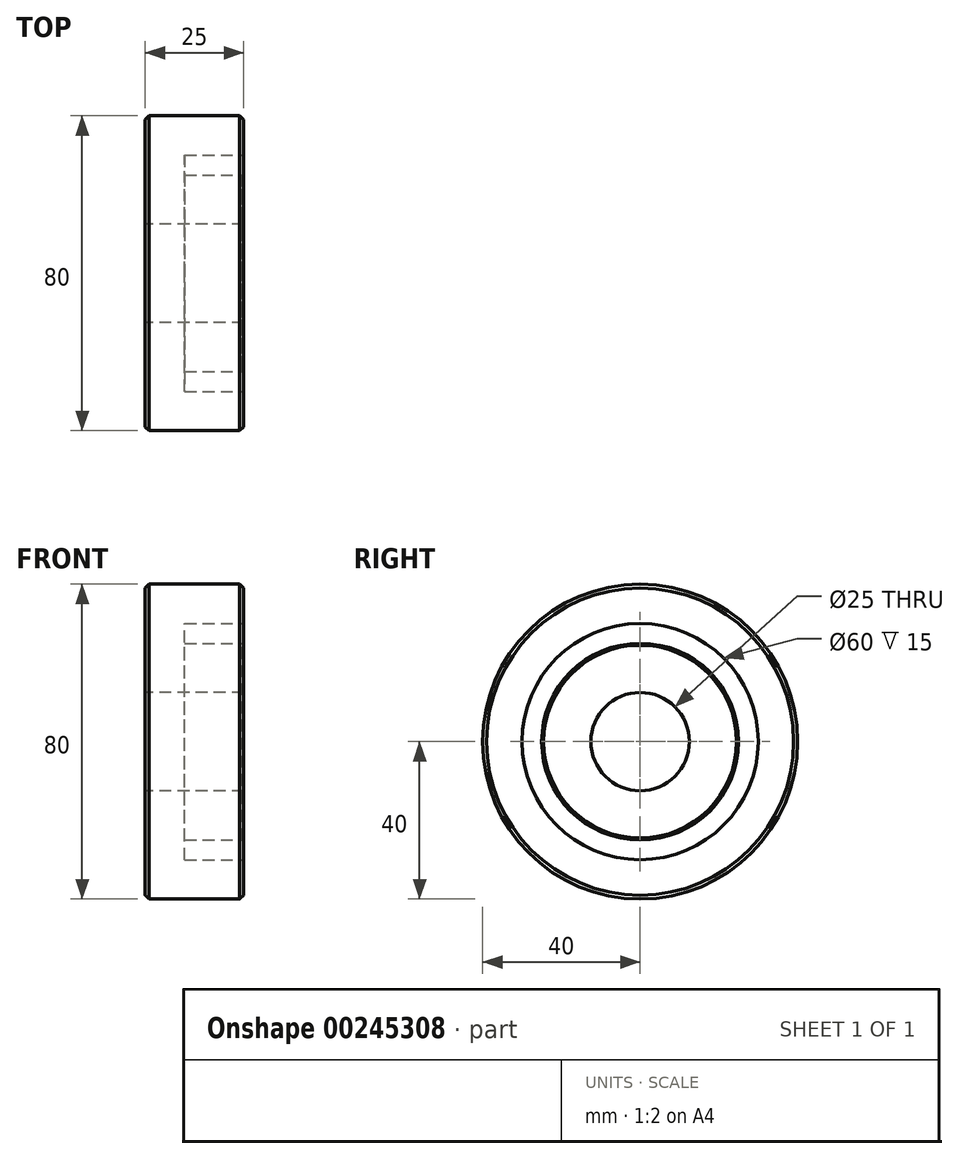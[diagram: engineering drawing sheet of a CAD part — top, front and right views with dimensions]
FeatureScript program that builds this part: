
annotation { "Feature Type Name" : "Feature", "Feature Type Description" : "" }
export const myFeature = defineFeature(function(context is Context, id is Id, definition is map)
    precondition{}
    {
        {
            var Q0;
            Q0=qCreatedBy(makeId("Right.planeOp"),FACE);
            var sketch = newSketch(context, id + "F0", { "sketchPlane" : qUnion([Q0])});
            skCircle(sketch, "E0", {"center": v(0, 0) * mm, "radius": 40 * mm});
            skSolve(sketch);
        }
        {
            var Q0;
            Q0 = qSketchRegion(id + "F0", true);
            extrude(context, id + "F1", {"entities" : qUnion([Q0]), "depth" : 25 * mm, "offsetDistance" : 25 * mm});
        }
        {
            var Q0;
            Q0=makeQuery(id+"F1.opExtrude","CAP_FACE",FACE,{"disambiguationData":[OSD([sQuery(id+"F0.wireOp",EDGE,"E0")])],"isStart":true});
            var sketch = newSketch(context, id + "F2", { "sketchPlane" : qUnion([Q0])});
            skCircle(sketch, "E1", {"center": v(0, 0) * mm, "radius": 12.5 * mm});
            skSolve(sketch);
        }
        {
            var Q0;
            Q0 = qSketchRegion(id + "F2", true);
            extrude(context, id + "F3", {"entities" : qUnion([Q0]), "operationType" : NewBodyOperationType.REMOVE, "endBound" : BoundingType.THROUGH_ALL, "oppositeDirection" : true, "depth" : 100 * mm, "offsetDistance" : 25 * mm});
        }
        {
            var Q0;
            Q0=makeQuery(id+"F3.opExtrude","CAP_EDGE",EDGE,{"disambiguationData":[OSD([sQuery(id+"F2.wireOp",EDGE,"E1")])],"isStart":false});
            var Q1;
            Q1=makeQuery(id+"F1.opExtrude","CAP_EDGE",EDGE,{"disambiguationData":[OSD([sQuery(id+"F0.wireOp",EDGE,"E0")])],"isStart":true});
            chamfer(context, id + "F4", {"entities" : qUnion([Q0, Q1]), "width" : 1 * mm, "tangentPropagation" : true});
        }
        {
            var Q0;
            Q0=makeQuery(id+"F1.opExtrude","CAP_FACE",FACE,{"disambiguationData":[OSD([sQuery(id+"F0.wireOp",EDGE,"E0")])],"isStart":false});
            var sketch = newSketch(context, id + "F5", { "sketchPlane" : qUnion([Q0])});
            skCircle(sketch, "E2", {"center": v(0, 0) * mm, "radius": 25 * mm});
            skCircle(sketch, "E3", {"center": v(0, 0) * mm, "radius": 30 * mm});
            skSolve(sketch);
        }
        {
            var Q0;
            Q0 = qSketchRegion(id + "F5", true);
            extrude(context, id + "F6", {"entities" : qUnion([Q0]), "operationType" : NewBodyOperationType.REMOVE, "oppositeDirection" : true, "depth" : 15 * mm, "offsetDistance" : 25 * mm});
        }
        {
            var Q0;
            Q0=makeQuery(id+"F1.opExtrude","CAP_EDGE",EDGE,{"disambiguationData":[OSD([sQuery(id+"F0.wireOp",EDGE,"E0")])],"isStart":false});
            chamfer(context, id + "F7", {"entities" : qUnion([Q0]), "width" : 1 * mm, "tangentPropagation" : true});
        }
        {
            var Q0;
            Q0=makeQuery(id+"F6.boolean.opBoolean","COPY",EDGE,{"derivedFrom":makeQuery(id+"F6.opExtrude","CAP_EDGE",EDGE,{"disambiguationData":[OSD([sQuery(id+"F5.wireOp",EDGE,"E2")])],"isStart":true})});
            chamfer(context, id + "F8", {"entities" : qUnion([Q0]), "width" : .5 * mm, "tangentPropagation" : true});
        }
        {
            var Q0;
            Q0 = qSketchRegion(id + "F5", true);
            extrude(context, id + "F9", {"entities" : qUnion([Q0]), "operationType" : NewBodyOperationType.REMOVE, "oppositeDirection" : true, "depth" : 10 * mm, "offsetDistance" : 25 * mm});
        }
    });
